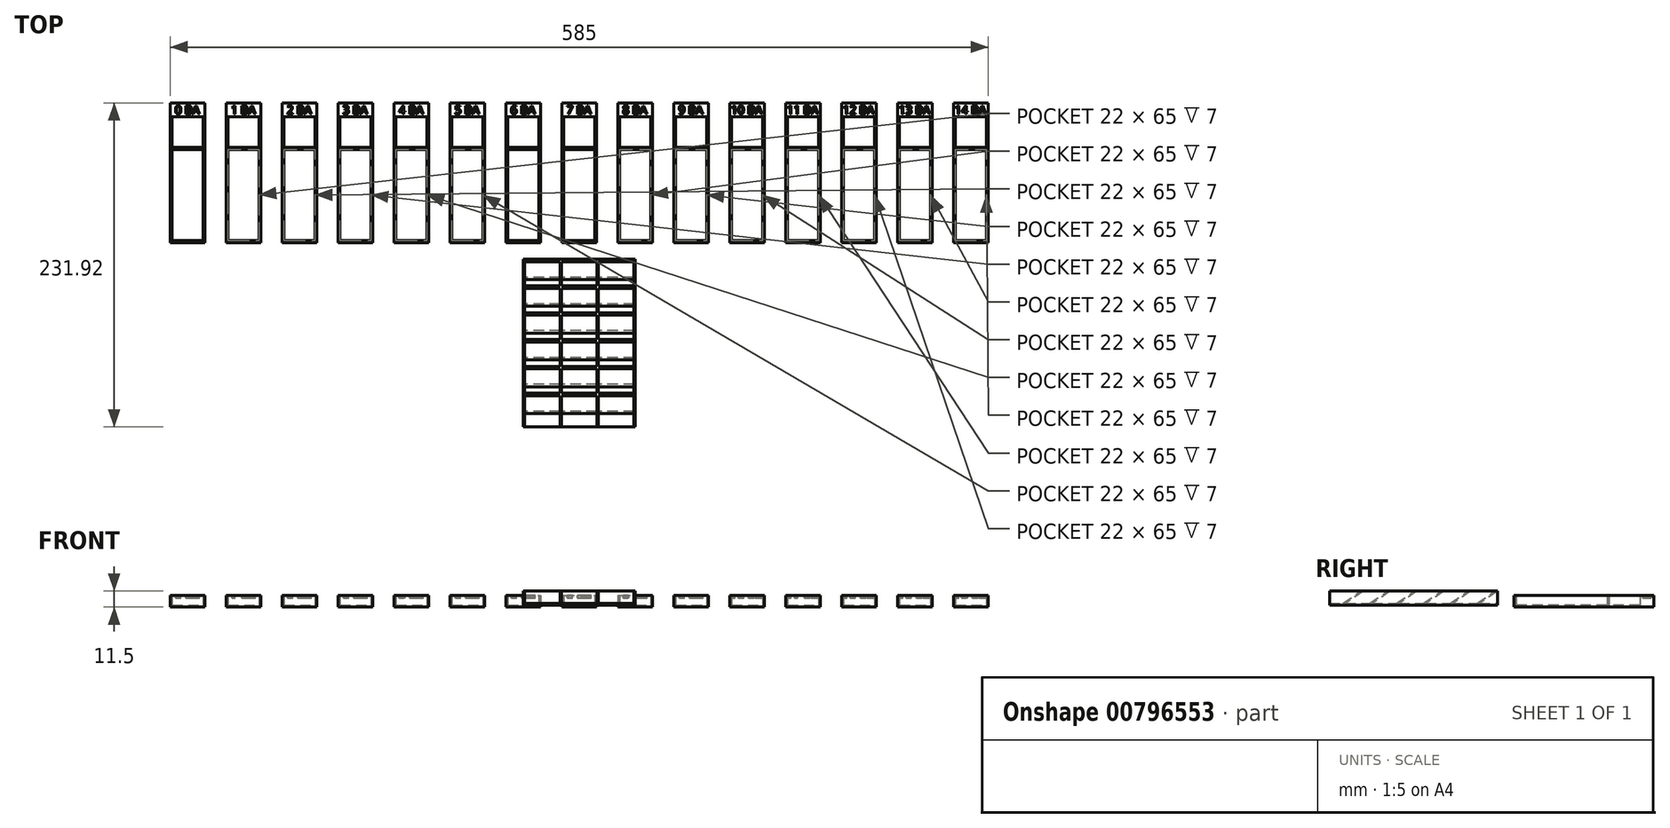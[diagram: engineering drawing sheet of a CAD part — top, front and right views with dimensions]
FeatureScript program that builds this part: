
annotation { "Feature Type Name" : "Feature", "Feature Type Description" : "" }
export const myFeature = defineFeature(function(context is Context, id is Id, definition is map)
    precondition{}
    {
        {
            var Q0;
            Q0=qCreatedBy(makeId("Top.planeOp"),FACE);
            var sketch = newSketch(context, id + "F0", { "sketchPlane" : qUnion([Q0])});
            skLineSegment(sketch, "E0.bottom", {"start": v(30.55, 66.22) * mm, "end": v(55.55, 66.22) * mm});
            skLineSegment(sketch, "E0.top", {"start": v(30.55, -33.78) * mm, "end": v(55.55, -33.78) * mm});
            skLineSegment(sketch, "E0.left", {"start": v(30.55, 66.22) * mm, "end": v(30.55, -33.78) * mm});
            skLineSegment(sketch, "E0.right", {"start": v(55.55, 66.22) * mm, "end": v(55.55, -33.78) * mm});
            skLineSegment(sketch, "E1.bottom", {"start": v(32.05, 56.22) * mm, "end": v(54.05, 56.22) * mm});
            skLineSegment(sketch, "E1.top", {"start": v(32.05, 34.22) * mm, "end": v(54.05, 34.22) * mm});
            skLineSegment(sketch, "E1.left", {"start": v(32.05, 56.22) * mm, "end": v(32.05, 34.22) * mm});
            skLineSegment(sketch, "E1.right", {"start": v(54.05, 56.22) * mm, "end": v(54.05, 34.22) * mm});
            skLineSegment(sketch, "E2.bottom", {"start": v(42.3, 32.72) * mm, "end": v(43.8, 32.72) * mm});
            skLineSegment(sketch, "E2.top", {"start": v(42.3, -32.28) * mm, "end": v(43.8, -32.28) * mm});
            skLineSegment(sketch, "E2.left", {"start": v(42.3, 32.72) * mm, "end": v(42.3, -32.28) * mm});
            skLineSegment(sketch, "E2.right", {"start": v(43.8, 32.72) * mm, "end": v(43.8, -32.28) * mm});
            skLineSegment(sketch, "E3.bottom", {"start": v(32.05, 32.72) * mm, "end": v(54.05, 32.72) * mm});
            skLineSegment(sketch, "E3.top", {"start": v(32.05, -32.28) * mm, "end": v(54.05, -32.28) * mm});
            skLineSegment(sketch, "E3.left", {"start": v(32.05, 32.72) * mm, "end": v(32.05, -32.28) * mm});
            skLineSegment(sketch, "E3.right", {"start": v(54.05, 32.72) * mm, "end": v(54.05, -32.28) * mm});
            skLineSegment(sketch, "E4", {"start": v(43.05, 66.22) * mm, "end": v(43.05, -33.78) * mm, "construction": true});
            skLineSegment(sketch, "E5.1.0.0", {"start": v(72.05, 34.22) * mm, "end": v(94.05, 34.22) * mm});
            skLineSegment(sketch, "E5.1.0.1", {"start": v(72.05, 56.22) * mm, "end": v(72.05, 34.22) * mm});
            skLineSegment(sketch, "E5.1.0.2", {"start": v(72.05, 32.72) * mm, "end": v(72.05, -32.28) * mm});
            skLineSegment(sketch, "E5.1.0.3", {"start": v(70.55, 66.22) * mm, "end": v(70.55, -33.78) * mm});
            skLineSegment(sketch, "E5.1.0.4", {"start": v(72.05, -32.28) * mm, "end": v(94.05, -32.28) * mm});
            skLineSegment(sketch, "E5.1.0.5", {"start": v(94.05, 32.72) * mm, "end": v(94.05, -32.28) * mm});
            skLineSegment(sketch, "E5.1.0.6", {"start": v(82.3, 32.72) * mm, "end": v(82.3, -32.28) * mm});
            skLineSegment(sketch, "E5.1.0.7", {"start": v(95.55, 66.22) * mm, "end": v(95.55, -33.78) * mm});
            skLineSegment(sketch, "E5.1.0.8", {"start": v(94.05, 56.22) * mm, "end": v(94.05, 34.22) * mm});
            skLineSegment(sketch, "E5.1.0.9", {"start": v(83.05, 66.22) * mm, "end": v(83.05, -33.78) * mm, "construction": true});
            skLineSegment(sketch, "E5.1.0.10", {"start": v(72.05, 32.72) * mm, "end": v(94.05, 32.72) * mm});
            skLineSegment(sketch, "E5.1.0.11", {"start": v(70.55, 66.22) * mm, "end": v(95.55, 66.22) * mm});
            skLineSegment(sketch, "E5.1.0.12", {"start": v(70.55, -33.78) * mm, "end": v(95.55, -33.78) * mm});
            skLineSegment(sketch, "E5.1.0.13", {"start": v(72.05, 56.22) * mm, "end": v(94.05, 56.22) * mm});
            skLineSegment(sketch, "E5.1.0.14", {"start": v(83.8, 32.72) * mm, "end": v(83.8, -32.28) * mm});
            skLineSegment(sketch, "E5.1.0.15", {"start": v(82.3, -32.28) * mm, "end": v(83.8, -32.28) * mm});
            skLineSegment(sketch, "E5.1.0.16", {"start": v(82.3, 32.72) * mm, "end": v(83.8, 32.72) * mm});
            skLineSegment(sketch, "E5.2.0.0", {"start": v(112.05, 34.22) * mm, "end": v(134.05, 34.22) * mm});
            skLineSegment(sketch, "E5.2.0.1", {"start": v(112.05, 56.22) * mm, "end": v(112.05, 34.22) * mm});
            skLineSegment(sketch, "E5.2.0.2", {"start": v(112.05, 32.72) * mm, "end": v(112.05, -32.28) * mm});
            skLineSegment(sketch, "E5.2.0.3", {"start": v(110.55, 66.22) * mm, "end": v(110.55, -33.78) * mm});
            skLineSegment(sketch, "E5.2.0.4", {"start": v(112.05, -32.28) * mm, "end": v(134.05, -32.28) * mm});
            skLineSegment(sketch, "E5.2.0.5", {"start": v(134.05, 32.72) * mm, "end": v(134.05, -32.28) * mm});
            skLineSegment(sketch, "E5.2.0.6", {"start": v(122.3, 32.72) * mm, "end": v(122.3, -32.28) * mm});
            skLineSegment(sketch, "E5.2.0.7", {"start": v(135.55, 66.22) * mm, "end": v(135.55, -33.78) * mm});
            skLineSegment(sketch, "E5.2.0.8", {"start": v(134.05, 56.22) * mm, "end": v(134.05, 34.22) * mm});
            skLineSegment(sketch, "E5.2.0.9", {"start": v(123.05, 66.22) * mm, "end": v(123.05, -33.78) * mm, "construction": true});
            skLineSegment(sketch, "E5.2.0.10", {"start": v(112.05, 32.72) * mm, "end": v(134.05, 32.72) * mm});
            skLineSegment(sketch, "E5.2.0.11", {"start": v(110.55, 66.22) * mm, "end": v(135.55, 66.22) * mm});
            skLineSegment(sketch, "E5.2.0.12", {"start": v(110.55, -33.78) * mm, "end": v(135.55, -33.78) * mm});
            skLineSegment(sketch, "E5.2.0.13", {"start": v(112.05, 56.22) * mm, "end": v(134.05, 56.22) * mm});
            skLineSegment(sketch, "E5.2.0.14", {"start": v(123.8, 32.72) * mm, "end": v(123.8, -32.28) * mm});
            skLineSegment(sketch, "E5.2.0.15", {"start": v(122.3, -32.28) * mm, "end": v(123.8, -32.28) * mm});
            skLineSegment(sketch, "E5.2.0.16", {"start": v(122.3, 32.72) * mm, "end": v(123.8, 32.72) * mm});
            skLineSegment(sketch, "E5.direction1", {"start": v(30.55, -33.78) * mm, "end": v(70.55, -33.78) * mm, "construction": true});
            skLineSegment(sketch, "E6.0.3.0", {"start": v(152.05, 34.22) * mm, "end": v(174.05, 34.22) * mm});
            skLineSegment(sketch, "E6.3.3.0", {"start": v(152.05, 56.22) * mm, "end": v(152.05, 34.22) * mm});
            skLineSegment(sketch, "E6.6.3.0", {"start": v(152.05, 32.72) * mm, "end": v(152.05, -32.28) * mm});
            skLineSegment(sketch, "E6.9.3.0", {"start": v(150.55, 66.22) * mm, "end": v(150.55, -33.78) * mm});
            skLineSegment(sketch, "E6.12.3.0", {"start": v(152.05, -32.28) * mm, "end": v(174.05, -32.28) * mm});
            skLineSegment(sketch, "E6.15.3.0", {"start": v(174.05, 32.72) * mm, "end": v(174.05, -32.28) * mm});
            skLineSegment(sketch, "E6.18.3.0", {"start": v(162.3, 32.72) * mm, "end": v(162.3, -32.28) * mm});
            skLineSegment(sketch, "E6.21.3.0", {"start": v(175.55, 66.22) * mm, "end": v(175.55, -33.78) * mm});
            skLineSegment(sketch, "E6.24.3.0", {"start": v(174.05, 56.22) * mm, "end": v(174.05, 34.22) * mm});
            skLineSegment(sketch, "E6.27.3.0", {"start": v(163.05, 66.22) * mm, "end": v(163.05, -33.78) * mm, "construction": true});
            skLineSegment(sketch, "E6.30.3.0", {"start": v(152.05, 32.72) * mm, "end": v(174.05, 32.72) * mm});
            skLineSegment(sketch, "E6.33.3.0", {"start": v(150.55, 66.22) * mm, "end": v(175.55, 66.22) * mm});
            skLineSegment(sketch, "E6.36.3.0", {"start": v(150.55, -33.78) * mm, "end": v(175.55, -33.78) * mm});
            skLineSegment(sketch, "E6.39.3.0", {"start": v(152.05, 56.22) * mm, "end": v(174.05, 56.22) * mm});
            skLineSegment(sketch, "E6.42.3.0", {"start": v(163.8, 32.72) * mm, "end": v(163.8, -32.28) * mm});
            skLineSegment(sketch, "E6.45.3.0", {"start": v(162.3, -32.28) * mm, "end": v(163.8, -32.28) * mm});
            skLineSegment(sketch, "E6.48.3.0", {"start": v(162.3, 32.72) * mm, "end": v(163.8, 32.72) * mm});
            skLineSegment(sketch, "E6.0.4.0", {"start": v(192.05, 34.22) * mm, "end": v(214.05, 34.22) * mm});
            skLineSegment(sketch, "E6.3.4.0", {"start": v(192.05, 56.22) * mm, "end": v(192.05, 34.22) * mm});
            skLineSegment(sketch, "E6.6.4.0", {"start": v(192.05, 32.72) * mm, "end": v(192.05, -32.28) * mm});
            skLineSegment(sketch, "E6.9.4.0", {"start": v(190.55, 66.22) * mm, "end": v(190.55, -33.78) * mm});
            skLineSegment(sketch, "E6.12.4.0", {"start": v(192.05, -32.28) * mm, "end": v(214.05, -32.28) * mm});
            skLineSegment(sketch, "E6.15.4.0", {"start": v(214.05, 32.72) * mm, "end": v(214.05, -32.28) * mm});
            skLineSegment(sketch, "E6.18.4.0", {"start": v(202.3, 32.72) * mm, "end": v(202.3, -32.28) * mm});
            skLineSegment(sketch, "E6.21.4.0", {"start": v(215.55, 66.22) * mm, "end": v(215.55, -33.78) * mm});
            skLineSegment(sketch, "E6.24.4.0", {"start": v(214.05, 56.22) * mm, "end": v(214.05, 34.22) * mm});
            skLineSegment(sketch, "E6.27.4.0", {"start": v(203.05, 66.22) * mm, "end": v(203.05, -33.78) * mm, "construction": true});
            skLineSegment(sketch, "E6.30.4.0", {"start": v(192.05, 32.72) * mm, "end": v(214.05, 32.72) * mm});
            skLineSegment(sketch, "E6.33.4.0", {"start": v(190.55, 66.22) * mm, "end": v(215.55, 66.22) * mm});
            skLineSegment(sketch, "E6.36.4.0", {"start": v(190.55, -33.78) * mm, "end": v(215.55, -33.78) * mm});
            skLineSegment(sketch, "E6.39.4.0", {"start": v(192.05, 56.22) * mm, "end": v(214.05, 56.22) * mm});
            skLineSegment(sketch, "E6.42.4.0", {"start": v(203.8, 32.72) * mm, "end": v(203.8, -32.28) * mm});
            skLineSegment(sketch, "E6.45.4.0", {"start": v(202.3, -32.28) * mm, "end": v(203.8, -32.28) * mm});
            skLineSegment(sketch, "E6.48.4.0", {"start": v(202.3, 32.72) * mm, "end": v(203.8, 32.72) * mm});
            skLineSegment(sketch, "E6.0.5.0", {"start": v(232.05, 34.22) * mm, "end": v(254.05, 34.22) * mm});
            skLineSegment(sketch, "E6.3.5.0", {"start": v(232.05, 56.22) * mm, "end": v(232.05, 34.22) * mm});
            skLineSegment(sketch, "E6.6.5.0", {"start": v(232.05, 32.72) * mm, "end": v(232.05, -32.28) * mm});
            skLineSegment(sketch, "E6.9.5.0", {"start": v(230.55, 66.22) * mm, "end": v(230.55, -33.78) * mm});
            skLineSegment(sketch, "E6.12.5.0", {"start": v(232.05, -32.28) * mm, "end": v(254.05, -32.28) * mm});
            skLineSegment(sketch, "E6.15.5.0", {"start": v(254.05, 32.72) * mm, "end": v(254.05, -32.28) * mm});
            skLineSegment(sketch, "E6.18.5.0", {"start": v(242.3, 32.72) * mm, "end": v(242.3, -32.28) * mm});
            skLineSegment(sketch, "E6.21.5.0", {"start": v(255.55, 66.22) * mm, "end": v(255.55, -33.78) * mm});
            skLineSegment(sketch, "E6.24.5.0", {"start": v(254.05, 56.22) * mm, "end": v(254.05, 34.22) * mm});
            skLineSegment(sketch, "E6.27.5.0", {"start": v(243.05, 66.22) * mm, "end": v(243.05, -33.78) * mm, "construction": true});
            skLineSegment(sketch, "E6.30.5.0", {"start": v(232.05, 32.72) * mm, "end": v(254.05, 32.72) * mm});
            skLineSegment(sketch, "E6.33.5.0", {"start": v(230.55, 66.22) * mm, "end": v(255.55, 66.22) * mm});
            skLineSegment(sketch, "E6.36.5.0", {"start": v(230.55, -33.78) * mm, "end": v(255.55, -33.78) * mm});
            skLineSegment(sketch, "E6.39.5.0", {"start": v(232.05, 56.22) * mm, "end": v(254.05, 56.22) * mm});
            skLineSegment(sketch, "E6.42.5.0", {"start": v(243.8, 32.72) * mm, "end": v(243.8, -32.28) * mm});
            skLineSegment(sketch, "E6.45.5.0", {"start": v(242.3, -32.28) * mm, "end": v(243.8, -32.28) * mm});
            skLineSegment(sketch, "E6.48.5.0", {"start": v(242.3, 32.72) * mm, "end": v(243.8, 32.72) * mm});
            skLineSegment(sketch, "E6.0.6.0", {"start": v(272.05, 34.22) * mm, "end": v(294.05, 34.22) * mm});
            skLineSegment(sketch, "E6.3.6.0", {"start": v(272.05, 56.22) * mm, "end": v(272.05, 34.22) * mm});
            skLineSegment(sketch, "E6.6.6.0", {"start": v(272.05, 32.72) * mm, "end": v(272.05, -32.28) * mm});
            skLineSegment(sketch, "E6.9.6.0", {"start": v(270.55, 66.22) * mm, "end": v(270.55, -33.78) * mm});
            skLineSegment(sketch, "E6.12.6.0", {"start": v(272.05, -32.28) * mm, "end": v(294.05, -32.28) * mm});
            skLineSegment(sketch, "E6.15.6.0", {"start": v(294.05, 32.72) * mm, "end": v(294.05, -32.28) * mm});
            skLineSegment(sketch, "E6.18.6.0", {"start": v(282.3, 32.72) * mm, "end": v(282.3, -32.28) * mm});
            skLineSegment(sketch, "E6.21.6.0", {"start": v(295.55, 66.22) * mm, "end": v(295.55, -33.78) * mm});
            skLineSegment(sketch, "E6.24.6.0", {"start": v(294.05, 56.22) * mm, "end": v(294.05, 34.22) * mm});
            skLineSegment(sketch, "E6.27.6.0", {"start": v(283.05, 66.22) * mm, "end": v(283.05, -33.78) * mm, "construction": true});
            skLineSegment(sketch, "E6.30.6.0", {"start": v(272.05, 32.72) * mm, "end": v(294.05, 32.72) * mm});
            skLineSegment(sketch, "E6.33.6.0", {"start": v(270.55, 66.22) * mm, "end": v(295.55, 66.22) * mm});
            skLineSegment(sketch, "E6.36.6.0", {"start": v(270.55, -33.78) * mm, "end": v(295.55, -33.78) * mm});
            skLineSegment(sketch, "E6.39.6.0", {"start": v(272.05, 56.22) * mm, "end": v(294.05, 56.22) * mm});
            skLineSegment(sketch, "E6.42.6.0", {"start": v(283.8, 32.72) * mm, "end": v(283.8, -32.28) * mm});
            skLineSegment(sketch, "E6.45.6.0", {"start": v(282.3, -32.28) * mm, "end": v(283.8, -32.28) * mm});
            skLineSegment(sketch, "E6.48.6.0", {"start": v(282.3, 32.72) * mm, "end": v(283.8, 32.72) * mm});
            skLineSegment(sketch, "E6.0.7.0", {"start": v(312.05, 34.22) * mm, "end": v(334.05, 34.22) * mm});
            skLineSegment(sketch, "E6.3.7.0", {"start": v(312.05, 56.22) * mm, "end": v(312.05, 34.22) * mm});
            skLineSegment(sketch, "E6.6.7.0", {"start": v(312.05, 32.72) * mm, "end": v(312.05, -32.28) * mm});
            skLineSegment(sketch, "E6.9.7.0", {"start": v(310.55, 66.22) * mm, "end": v(310.55, -33.78) * mm});
            skLineSegment(sketch, "E6.12.7.0", {"start": v(312.05, -32.28) * mm, "end": v(334.05, -32.28) * mm});
            skLineSegment(sketch, "E6.15.7.0", {"start": v(334.05, 32.72) * mm, "end": v(334.05, -32.28) * mm});
            skLineSegment(sketch, "E6.18.7.0", {"start": v(322.3, 32.72) * mm, "end": v(322.3, -32.28) * mm});
            skLineSegment(sketch, "E6.21.7.0", {"start": v(335.55, 66.22) * mm, "end": v(335.55, -33.78) * mm});
            skLineSegment(sketch, "E6.24.7.0", {"start": v(334.05, 56.22) * mm, "end": v(334.05, 34.22) * mm});
            skLineSegment(sketch, "E6.27.7.0", {"start": v(323.05, 66.22) * mm, "end": v(323.05, -33.78) * mm, "construction": true});
            skLineSegment(sketch, "E6.30.7.0", {"start": v(312.05, 32.72) * mm, "end": v(334.05, 32.72) * mm});
            skLineSegment(sketch, "E6.33.7.0", {"start": v(310.55, 66.22) * mm, "end": v(335.55, 66.22) * mm});
            skLineSegment(sketch, "E6.36.7.0", {"start": v(310.55, -33.78) * mm, "end": v(335.55, -33.78) * mm});
            skLineSegment(sketch, "E6.39.7.0", {"start": v(312.05, 56.22) * mm, "end": v(334.05, 56.22) * mm});
            skLineSegment(sketch, "E6.42.7.0", {"start": v(323.8, 32.72) * mm, "end": v(323.8, -32.28) * mm});
            skLineSegment(sketch, "E6.45.7.0", {"start": v(322.3, -32.28) * mm, "end": v(323.8, -32.28) * mm});
            skLineSegment(sketch, "E6.48.7.0", {"start": v(322.3, 32.72) * mm, "end": v(323.8, 32.72) * mm});
            skLineSegment(sketch, "E6.0.8.0", {"start": v(352.05, 34.22) * mm, "end": v(374.05, 34.22) * mm});
            skLineSegment(sketch, "E6.3.8.0", {"start": v(352.05, 56.22) * mm, "end": v(352.05, 34.22) * mm});
            skLineSegment(sketch, "E6.6.8.0", {"start": v(352.05, 32.72) * mm, "end": v(352.05, -32.28) * mm});
            skLineSegment(sketch, "E6.9.8.0", {"start": v(350.55, 66.22) * mm, "end": v(350.55, -33.78) * mm});
            skLineSegment(sketch, "E6.12.8.0", {"start": v(352.05, -32.28) * mm, "end": v(374.05, -32.28) * mm});
            skLineSegment(sketch, "E6.15.8.0", {"start": v(374.05, 32.72) * mm, "end": v(374.05, -32.28) * mm});
            skLineSegment(sketch, "E6.18.8.0", {"start": v(362.3, 32.72) * mm, "end": v(362.3, -32.28) * mm});
            skLineSegment(sketch, "E6.21.8.0", {"start": v(375.55, 66.22) * mm, "end": v(375.55, -33.78) * mm});
            skLineSegment(sketch, "E6.24.8.0", {"start": v(374.05, 56.22) * mm, "end": v(374.05, 34.22) * mm});
            skLineSegment(sketch, "E6.27.8.0", {"start": v(363.05, 66.22) * mm, "end": v(363.05, -33.78) * mm, "construction": true});
            skLineSegment(sketch, "E6.30.8.0", {"start": v(352.05, 32.72) * mm, "end": v(374.05, 32.72) * mm});
            skLineSegment(sketch, "E6.33.8.0", {"start": v(350.55, 66.22) * mm, "end": v(375.55, 66.22) * mm});
            skLineSegment(sketch, "E6.36.8.0", {"start": v(350.55, -33.78) * mm, "end": v(375.55, -33.78) * mm});
            skLineSegment(sketch, "E6.39.8.0", {"start": v(352.05, 56.22) * mm, "end": v(374.05, 56.22) * mm});
            skLineSegment(sketch, "E6.42.8.0", {"start": v(363.8, 32.72) * mm, "end": v(363.8, -32.28) * mm});
            skLineSegment(sketch, "E6.45.8.0", {"start": v(362.3, -32.28) * mm, "end": v(363.8, -32.28) * mm});
            skLineSegment(sketch, "E6.48.8.0", {"start": v(362.3, 32.72) * mm, "end": v(363.8, 32.72) * mm});
            skLineSegment(sketch, "E6.0.9.0", {"start": v(392.05, 34.22) * mm, "end": v(414.05, 34.22) * mm});
            skLineSegment(sketch, "E6.3.9.0", {"start": v(392.05, 56.22) * mm, "end": v(392.05, 34.22) * mm});
            skLineSegment(sketch, "E6.6.9.0", {"start": v(392.05, 32.72) * mm, "end": v(392.05, -32.28) * mm});
            skLineSegment(sketch, "E6.9.9.0", {"start": v(390.55, 66.22) * mm, "end": v(390.55, -33.78) * mm});
            skLineSegment(sketch, "E6.12.9.0", {"start": v(392.05, -32.28) * mm, "end": v(414.05, -32.28) * mm});
            skLineSegment(sketch, "E6.15.9.0", {"start": v(414.05, 32.72) * mm, "end": v(414.05, -32.28) * mm});
            skLineSegment(sketch, "E6.18.9.0", {"start": v(402.3, 32.72) * mm, "end": v(402.3, -32.28) * mm});
            skLineSegment(sketch, "E6.21.9.0", {"start": v(415.55, 66.22) * mm, "end": v(415.55, -33.78) * mm});
            skLineSegment(sketch, "E6.24.9.0", {"start": v(414.05, 56.22) * mm, "end": v(414.05, 34.22) * mm});
            skLineSegment(sketch, "E6.27.9.0", {"start": v(403.05, 66.22) * mm, "end": v(403.05, -33.78) * mm, "construction": true});
            skLineSegment(sketch, "E6.30.9.0", {"start": v(392.05, 32.72) * mm, "end": v(414.05, 32.72) * mm});
            skLineSegment(sketch, "E6.33.9.0", {"start": v(390.55, 66.22) * mm, "end": v(415.55, 66.22) * mm});
            skLineSegment(sketch, "E6.36.9.0", {"start": v(390.55, -33.78) * mm, "end": v(415.55, -33.78) * mm});
            skLineSegment(sketch, "E6.39.9.0", {"start": v(392.05, 56.22) * mm, "end": v(414.05, 56.22) * mm});
            skLineSegment(sketch, "E6.42.9.0", {"start": v(403.8, 32.72) * mm, "end": v(403.8, -32.28) * mm});
            skLineSegment(sketch, "E6.45.9.0", {"start": v(402.3, -32.28) * mm, "end": v(403.8, -32.28) * mm});
            skLineSegment(sketch, "E6.48.9.0", {"start": v(402.3, 32.72) * mm, "end": v(403.8, 32.72) * mm});
            skLineSegment(sketch, "E6.0.10.0", {"start": v(432.05, 34.22) * mm, "end": v(454.05, 34.22) * mm});
            skLineSegment(sketch, "E6.3.10.0", {"start": v(432.05, 56.22) * mm, "end": v(432.05, 34.22) * mm});
            skLineSegment(sketch, "E6.6.10.0", {"start": v(432.05, 32.72) * mm, "end": v(432.05, -32.28) * mm});
            skLineSegment(sketch, "E6.9.10.0", {"start": v(430.55, 66.22) * mm, "end": v(430.55, -33.78) * mm});
            skLineSegment(sketch, "E6.12.10.0", {"start": v(432.05, -32.28) * mm, "end": v(454.05, -32.28) * mm});
            skLineSegment(sketch, "E6.15.10.0", {"start": v(454.05, 32.72) * mm, "end": v(454.05, -32.28) * mm});
            skLineSegment(sketch, "E6.18.10.0", {"start": v(442.3, 32.72) * mm, "end": v(442.3, -32.28) * mm});
            skLineSegment(sketch, "E6.21.10.0", {"start": v(455.55, 66.22) * mm, "end": v(455.55, -33.78) * mm});
            skLineSegment(sketch, "E6.24.10.0", {"start": v(454.05, 56.22) * mm, "end": v(454.05, 34.22) * mm});
            skLineSegment(sketch, "E6.27.10.0", {"start": v(443.05, 66.22) * mm, "end": v(443.05, -33.78) * mm, "construction": true});
            skLineSegment(sketch, "E6.30.10.0", {"start": v(432.05, 32.72) * mm, "end": v(454.05, 32.72) * mm});
            skLineSegment(sketch, "E6.33.10.0", {"start": v(430.55, 66.22) * mm, "end": v(455.55, 66.22) * mm});
            skLineSegment(sketch, "E6.36.10.0", {"start": v(430.55, -33.78) * mm, "end": v(455.55, -33.78) * mm});
            skLineSegment(sketch, "E6.39.10.0", {"start": v(432.05, 56.22) * mm, "end": v(454.05, 56.22) * mm});
            skLineSegment(sketch, "E6.42.10.0", {"start": v(443.8, 32.72) * mm, "end": v(443.8, -32.28) * mm});
            skLineSegment(sketch, "E6.45.10.0", {"start": v(442.3, -32.28) * mm, "end": v(443.8, -32.28) * mm});
            skLineSegment(sketch, "E6.48.10.0", {"start": v(442.3, 32.72) * mm, "end": v(443.8, 32.72) * mm});
            skLineSegment(sketch, "E6.0.11.0", {"start": v(472.05, 34.22) * mm, "end": v(494.05, 34.22) * mm});
            skLineSegment(sketch, "E6.3.11.0", {"start": v(472.05, 56.22) * mm, "end": v(472.05, 34.22) * mm});
            skLineSegment(sketch, "E6.6.11.0", {"start": v(472.05, 32.72) * mm, "end": v(472.05, -32.28) * mm});
            skLineSegment(sketch, "E6.9.11.0", {"start": v(470.55, 66.22) * mm, "end": v(470.55, -33.78) * mm});
            skLineSegment(sketch, "E6.12.11.0", {"start": v(472.05, -32.28) * mm, "end": v(494.05, -32.28) * mm});
            skLineSegment(sketch, "E6.15.11.0", {"start": v(494.05, 32.72) * mm, "end": v(494.05, -32.28) * mm});
            skLineSegment(sketch, "E6.18.11.0", {"start": v(482.3, 32.72) * mm, "end": v(482.3, -32.28) * mm});
            skLineSegment(sketch, "E6.21.11.0", {"start": v(495.55, 66.22) * mm, "end": v(495.55, -33.78) * mm});
            skLineSegment(sketch, "E6.24.11.0", {"start": v(494.05, 56.22) * mm, "end": v(494.05, 34.22) * mm});
            skLineSegment(sketch, "E6.27.11.0", {"start": v(483.05, 66.22) * mm, "end": v(483.05, -33.78) * mm, "construction": true});
            skLineSegment(sketch, "E6.30.11.0", {"start": v(472.05, 32.72) * mm, "end": v(494.05, 32.72) * mm});
            skLineSegment(sketch, "E6.33.11.0", {"start": v(470.55, 66.22) * mm, "end": v(495.55, 66.22) * mm});
            skLineSegment(sketch, "E6.36.11.0", {"start": v(470.55, -33.78) * mm, "end": v(495.55, -33.78) * mm});
            skLineSegment(sketch, "E6.39.11.0", {"start": v(472.05, 56.22) * mm, "end": v(494.05, 56.22) * mm});
            skLineSegment(sketch, "E6.42.11.0", {"start": v(483.8, 32.72) * mm, "end": v(483.8, -32.28) * mm});
            skLineSegment(sketch, "E6.45.11.0", {"start": v(482.3, -32.28) * mm, "end": v(483.8, -32.28) * mm});
            skLineSegment(sketch, "E6.48.11.0", {"start": v(482.3, 32.72) * mm, "end": v(483.8, 32.72) * mm});
            skLineSegment(sketch, "E7.0.12.0", {"start": v(512.05, 34.22) * mm, "end": v(534.05, 34.22) * mm});
            skLineSegment(sketch, "E7.3.12.0", {"start": v(512.05, 56.22) * mm, "end": v(512.05, 34.22) * mm});
            skLineSegment(sketch, "E7.6.12.0", {"start": v(512.05, 32.72) * mm, "end": v(512.05, -32.28) * mm});
            skLineSegment(sketch, "E7.9.12.0", {"start": v(510.55, 66.22) * mm, "end": v(510.55, -33.78) * mm});
            skLineSegment(sketch, "E7.12.12.0", {"start": v(512.05, -32.28) * mm, "end": v(534.05, -32.28) * mm});
            skLineSegment(sketch, "E7.15.12.0", {"start": v(534.05, 32.72) * mm, "end": v(534.05, -32.28) * mm});
            skLineSegment(sketch, "E7.18.12.0", {"start": v(522.3, 32.72) * mm, "end": v(522.3, -32.28) * mm});
            skLineSegment(sketch, "E7.21.12.0", {"start": v(535.55, 66.22) * mm, "end": v(535.55, -33.78) * mm});
            skLineSegment(sketch, "E7.24.12.0", {"start": v(534.05, 56.22) * mm, "end": v(534.05, 34.22) * mm});
            skLineSegment(sketch, "E7.27.12.0", {"start": v(523.05, 66.22) * mm, "end": v(523.05, -33.78) * mm, "construction": true});
            skLineSegment(sketch, "E7.30.12.0", {"start": v(512.05, 32.72) * mm, "end": v(534.05, 32.72) * mm});
            skLineSegment(sketch, "E7.33.12.0", {"start": v(510.55, 66.22) * mm, "end": v(535.55, 66.22) * mm});
            skLineSegment(sketch, "E7.36.12.0", {"start": v(510.55, -33.78) * mm, "end": v(535.55, -33.78) * mm});
            skLineSegment(sketch, "E7.39.12.0", {"start": v(512.05, 56.22) * mm, "end": v(534.05, 56.22) * mm});
            skLineSegment(sketch, "E7.42.12.0", {"start": v(523.8, 32.72) * mm, "end": v(523.8, -32.28) * mm});
            skLineSegment(sketch, "E7.45.12.0", {"start": v(522.3, -32.28) * mm, "end": v(523.8, -32.28) * mm});
            skLineSegment(sketch, "E7.48.12.0", {"start": v(522.3, 32.72) * mm, "end": v(523.8, 32.72) * mm});
            skLineSegment(sketch, "E8.0.13.0", {"start": v(552.05, 34.22) * mm, "end": v(574.05, 34.22) * mm});
            skLineSegment(sketch, "E8.3.13.0", {"start": v(552.05, 56.22) * mm, "end": v(552.05, 34.22) * mm});
            skLineSegment(sketch, "E8.6.13.0", {"start": v(552.05, 32.72) * mm, "end": v(552.05, -32.28) * mm});
            skLineSegment(sketch, "E8.9.13.0", {"start": v(550.55, 66.22) * mm, "end": v(550.55, -33.78) * mm});
            skLineSegment(sketch, "E8.12.13.0", {"start": v(552.05, -32.28) * mm, "end": v(574.05, -32.28) * mm});
            skLineSegment(sketch, "E8.15.13.0", {"start": v(574.05, 32.72) * mm, "end": v(574.05, -32.28) * mm});
            skLineSegment(sketch, "E8.18.13.0", {"start": v(562.3, 32.72) * mm, "end": v(562.3, -32.28) * mm});
            skLineSegment(sketch, "E8.21.13.0", {"start": v(575.55, 66.22) * mm, "end": v(575.55, -33.78) * mm});
            skLineSegment(sketch, "E8.24.13.0", {"start": v(574.05, 56.22) * mm, "end": v(574.05, 34.22) * mm});
            skLineSegment(sketch, "E8.27.13.0", {"start": v(563.05, 66.22) * mm, "end": v(563.05, -33.78) * mm, "construction": true});
            skLineSegment(sketch, "E8.30.13.0", {"start": v(552.05, 32.72) * mm, "end": v(574.05, 32.72) * mm});
            skLineSegment(sketch, "E8.33.13.0", {"start": v(550.55, 66.22) * mm, "end": v(575.55, 66.22) * mm});
            skLineSegment(sketch, "E8.36.13.0", {"start": v(550.55, -33.78) * mm, "end": v(575.55, -33.78) * mm});
            skLineSegment(sketch, "E8.39.13.0", {"start": v(552.05, 56.22) * mm, "end": v(574.05, 56.22) * mm});
            skLineSegment(sketch, "E8.42.13.0", {"start": v(563.8, 32.72) * mm, "end": v(563.8, -32.28) * mm});
            skLineSegment(sketch, "E8.45.13.0", {"start": v(562.3, -32.28) * mm, "end": v(563.8, -32.28) * mm});
            skLineSegment(sketch, "E8.48.13.0", {"start": v(562.3, 32.72) * mm, "end": v(563.8, 32.72) * mm});
            skLineSegment(sketch, "E8.0.14.0", {"start": v(592.05, 34.22) * mm, "end": v(614.05, 34.22) * mm});
            skLineSegment(sketch, "E8.3.14.0", {"start": v(592.05, 56.22) * mm, "end": v(592.05, 34.22) * mm});
            skLineSegment(sketch, "E8.6.14.0", {"start": v(592.05, 32.72) * mm, "end": v(592.05, -32.28) * mm});
            skLineSegment(sketch, "E8.9.14.0", {"start": v(590.55, 66.22) * mm, "end": v(590.55, -33.78) * mm});
            skLineSegment(sketch, "E8.12.14.0", {"start": v(592.05, -32.28) * mm, "end": v(614.05, -32.28) * mm});
            skLineSegment(sketch, "E8.15.14.0", {"start": v(614.05, 32.72) * mm, "end": v(614.05, -32.28) * mm});
            skLineSegment(sketch, "E8.18.14.0", {"start": v(602.3, 32.72) * mm, "end": v(602.3, -32.28) * mm});
            skLineSegment(sketch, "E8.21.14.0", {"start": v(615.55, 66.22) * mm, "end": v(615.55, -33.78) * mm});
            skLineSegment(sketch, "E8.24.14.0", {"start": v(614.05, 56.22) * mm, "end": v(614.05, 34.22) * mm});
            skLineSegment(sketch, "E8.27.14.0", {"start": v(603.05, 66.22) * mm, "end": v(603.05, -33.78) * mm, "construction": true});
            skLineSegment(sketch, "E8.30.14.0", {"start": v(592.05, 32.72) * mm, "end": v(614.05, 32.72) * mm});
            skLineSegment(sketch, "E8.33.14.0", {"start": v(590.55, 66.22) * mm, "end": v(615.55, 66.22) * mm});
            skLineSegment(sketch, "E8.36.14.0", {"start": v(590.55, -33.78) * mm, "end": v(615.55, -33.78) * mm});
            skLineSegment(sketch, "E8.39.14.0", {"start": v(592.05, 56.22) * mm, "end": v(614.05, 56.22) * mm});
            skLineSegment(sketch, "E8.42.14.0", {"start": v(603.8, 32.72) * mm, "end": v(603.8, -32.28) * mm});
            skLineSegment(sketch, "E8.45.14.0", {"start": v(602.3, -32.28) * mm, "end": v(603.8, -32.28) * mm});
            skLineSegment(sketch, "E8.48.14.0", {"start": v(602.3, 32.72) * mm, "end": v(603.8, 32.72) * mm});
            skSolve(sketch);
        }
        {
            var Q0;
            Q0=qCreatedBy(makeId("Top.planeOp"),FACE);
            var sketch = newSketch(context, id + "F1", { "sketchPlane" : qUnion([Q0])});
            skLineSegment(sketch, "E9.bottom", {"start": v(30.55, 66.22) * mm, "end": v(55.55, 66.22) * mm});
            skLineSegment(sketch, "E9.top", {"start": v(30.55, -33.78) * mm, "end": v(55.55, -33.78) * mm});
            skLineSegment(sketch, "E9.left", {"start": v(30.55, 66.22) * mm, "end": v(30.55, -33.78) * mm});
            skLineSegment(sketch, "E9.right", {"start": v(55.55, 66.22) * mm, "end": v(55.55, -33.78) * mm});
            skLineSegment(sketch, "E10.1.0.0", {"start": v(70.55, 66.22) * mm, "end": v(95.55, 66.22) * mm});
            skLineSegment(sketch, "E10.1.0.1", {"start": v(70.55, 66.22) * mm, "end": v(70.55, -33.78) * mm});
            skLineSegment(sketch, "E10.1.0.2", {"start": v(70.55, -33.78) * mm, "end": v(95.55, -33.78) * mm});
            skLineSegment(sketch, "E10.1.0.3", {"start": v(95.55, 66.22) * mm, "end": v(95.55, -33.78) * mm});
            skLineSegment(sketch, "E10.2.0.0", {"start": v(110.55, 66.22) * mm, "end": v(135.55, 66.22) * mm});
            skLineSegment(sketch, "E10.2.0.1", {"start": v(110.55, 66.22) * mm, "end": v(110.55, -33.78) * mm});
            skLineSegment(sketch, "E10.2.0.2", {"start": v(110.55, -33.78) * mm, "end": v(135.55, -33.78) * mm});
            skLineSegment(sketch, "E10.2.0.3", {"start": v(135.55, 66.22) * mm, "end": v(135.55, -33.78) * mm});
            skLineSegment(sketch, "E10.direction1", {"start": v(30.55, 66.22) * mm, "end": v(70.55, 66.22) * mm, "construction": true});
            skLineSegment(sketch, "E11.0.3.0", {"start": v(150.55, 66.22) * mm, "end": v(175.55, 66.22) * mm});
            skLineSegment(sketch, "E11.3.3.0", {"start": v(150.55, 66.22) * mm, "end": v(150.55, -33.78) * mm});
            skLineSegment(sketch, "E11.6.3.0", {"start": v(150.55, -33.78) * mm, "end": v(175.55, -33.78) * mm});
            skLineSegment(sketch, "E11.9.3.0", {"start": v(175.55, 66.22) * mm, "end": v(175.55, -33.78) * mm});
            skLineSegment(sketch, "E11.0.4.0", {"start": v(190.55, 66.22) * mm, "end": v(215.55, 66.22) * mm});
            skLineSegment(sketch, "E11.3.4.0", {"start": v(190.55, 66.22) * mm, "end": v(190.55, -33.78) * mm});
            skLineSegment(sketch, "E11.6.4.0", {"start": v(190.55, -33.78) * mm, "end": v(215.55, -33.78) * mm});
            skLineSegment(sketch, "E11.9.4.0", {"start": v(215.55, 66.22) * mm, "end": v(215.55, -33.78) * mm});
            skLineSegment(sketch, "E11.0.5.0", {"start": v(230.55, 66.22) * mm, "end": v(255.55, 66.22) * mm});
            skLineSegment(sketch, "E11.3.5.0", {"start": v(230.55, 66.22) * mm, "end": v(230.55, -33.78) * mm});
            skLineSegment(sketch, "E11.6.5.0", {"start": v(230.55, -33.78) * mm, "end": v(255.55, -33.78) * mm});
            skLineSegment(sketch, "E11.9.5.0", {"start": v(255.55, 66.22) * mm, "end": v(255.55, -33.78) * mm});
            skLineSegment(sketch, "E11.0.6.0", {"start": v(270.55, 66.22) * mm, "end": v(295.55, 66.22) * mm});
            skLineSegment(sketch, "E11.3.6.0", {"start": v(270.55, 66.22) * mm, "end": v(270.55, -33.78) * mm});
            skLineSegment(sketch, "E11.6.6.0", {"start": v(270.55, -33.78) * mm, "end": v(295.55, -33.78) * mm});
            skLineSegment(sketch, "E11.9.6.0", {"start": v(295.55, 66.22) * mm, "end": v(295.55, -33.78) * mm});
            skLineSegment(sketch, "E11.0.7.0", {"start": v(310.55, 66.22) * mm, "end": v(335.55, 66.22) * mm});
            skLineSegment(sketch, "E11.3.7.0", {"start": v(310.55, 66.22) * mm, "end": v(310.55, -33.78) * mm});
            skLineSegment(sketch, "E11.6.7.0", {"start": v(310.55, -33.78) * mm, "end": v(335.55, -33.78) * mm});
            skLineSegment(sketch, "E11.9.7.0", {"start": v(335.55, 66.22) * mm, "end": v(335.55, -33.78) * mm});
            skLineSegment(sketch, "E11.0.8.0", {"start": v(350.55, 66.22) * mm, "end": v(375.55, 66.22) * mm});
            skLineSegment(sketch, "E11.3.8.0", {"start": v(350.55, 66.22) * mm, "end": v(350.55, -33.78) * mm});
            skLineSegment(sketch, "E11.6.8.0", {"start": v(350.55, -33.78) * mm, "end": v(375.55, -33.78) * mm});
            skLineSegment(sketch, "E11.9.8.0", {"start": v(375.55, 66.22) * mm, "end": v(375.55, -33.78) * mm});
            skLineSegment(sketch, "E11.0.9.0", {"start": v(390.55, 66.22) * mm, "end": v(415.55, 66.22) * mm});
            skLineSegment(sketch, "E11.3.9.0", {"start": v(390.55, 66.22) * mm, "end": v(390.55, -33.78) * mm});
            skLineSegment(sketch, "E11.6.9.0", {"start": v(390.55, -33.78) * mm, "end": v(415.55, -33.78) * mm});
            skLineSegment(sketch, "E11.9.9.0", {"start": v(415.55, 66.22) * mm, "end": v(415.55, -33.78) * mm});
            skLineSegment(sketch, "E11.0.10.0", {"start": v(430.55, 66.22) * mm, "end": v(455.55, 66.22) * mm});
            skLineSegment(sketch, "E11.3.10.0", {"start": v(430.55, 66.22) * mm, "end": v(430.55, -33.78) * mm});
            skLineSegment(sketch, "E11.6.10.0", {"start": v(430.55, -33.78) * mm, "end": v(455.55, -33.78) * mm});
            skLineSegment(sketch, "E11.9.10.0", {"start": v(455.55, 66.22) * mm, "end": v(455.55, -33.78) * mm});
            skLineSegment(sketch, "E11.0.11.0", {"start": v(470.55, 66.22) * mm, "end": v(495.55, 66.22) * mm});
            skLineSegment(sketch, "E11.3.11.0", {"start": v(470.55, 66.22) * mm, "end": v(470.55, -33.78) * mm});
            skLineSegment(sketch, "E11.6.11.0", {"start": v(470.55, -33.78) * mm, "end": v(495.55, -33.78) * mm});
            skLineSegment(sketch, "E11.9.11.0", {"start": v(495.55, 66.22) * mm, "end": v(495.55, -33.78) * mm});
            skLineSegment(sketch, "E12.0.12.0", {"start": v(510.55, 66.22) * mm, "end": v(535.55, 66.22) * mm});
            skLineSegment(sketch, "E12.3.12.0", {"start": v(510.55, 66.22) * mm, "end": v(510.55, -33.78) * mm});
            skLineSegment(sketch, "E12.6.12.0", {"start": v(510.55, -33.78) * mm, "end": v(535.55, -33.78) * mm});
            skLineSegment(sketch, "E12.9.12.0", {"start": v(535.55, 66.22) * mm, "end": v(535.55, -33.78) * mm});
            skLineSegment(sketch, "E12.0.13.0", {"start": v(550.55, 66.22) * mm, "end": v(575.55, 66.22) * mm});
            skLineSegment(sketch, "E12.3.13.0", {"start": v(550.55, 66.22) * mm, "end": v(550.55, -33.78) * mm});
            skLineSegment(sketch, "E12.6.13.0", {"start": v(550.55, -33.78) * mm, "end": v(575.55, -33.78) * mm});
            skLineSegment(sketch, "E12.9.13.0", {"start": v(575.55, 66.22) * mm, "end": v(575.55, -33.78) * mm});
            skLineSegment(sketch, "E12.0.14.0", {"start": v(590.55, 66.22) * mm, "end": v(615.55, 66.22) * mm});
            skLineSegment(sketch, "E12.3.14.0", {"start": v(590.55, 66.22) * mm, "end": v(590.55, -33.78) * mm});
            skLineSegment(sketch, "E12.6.14.0", {"start": v(590.55, -33.78) * mm, "end": v(615.55, -33.78) * mm});
            skLineSegment(sketch, "E12.9.14.0", {"start": v(615.55, 66.22) * mm, "end": v(615.55, -33.78) * mm});
            skSolve(sketch);
        }
        {
            var Q0;
            {Q0=qUnion([makeQuery(id+"F0.imprint","IMPRINT",FACE,{"disambiguationData":[TD([[makeQuery(id+"F0.imprint","IMPRINT",EDGE,{"derivedFrom":sQuery(id+"F0.wireOp",EDGE,"E0.bottom")}),-1.0]])]}),makeQuery(id+"F0.imprint","IMPRINT",FACE,{"disambiguationData":[TD([[makeQuery(id+"F0.imprint","IMPRINT",EDGE,{"derivedFrom":sQuery(id+"F0.wireOp",EDGE,"E5.1.0.0")}),-1.0]])]}),makeQuery(id+"F0.imprint","IMPRINT",FACE,{"disambiguationData":[TD([[makeQuery(id+"F0.imprint","IMPRINT",EDGE,{"derivedFrom":sQuery(id+"F0.wireOp",EDGE,"E5.2.0.0")}),-1.0]])]}),makeQuery(id+"F0.imprint","IMPRINT",FACE,{"disambiguationData":[TD([[makeQuery(id+"F0.imprint","IMPRINT",EDGE,{"derivedFrom":sQuery(id+"F0.wireOp",EDGE,"E6.0.3.0")}),-1.0]])]}),makeQuery(id+"F0.imprint","IMPRINT",FACE,{"disambiguationData":[TD([[makeQuery(id+"F0.imprint","IMPRINT",EDGE,{"derivedFrom":sQuery(id+"F0.wireOp",EDGE,"E6.0.4.0")}),-1.0]])]}),makeQuery(id+"F0.imprint","IMPRINT",FACE,{"disambiguationData":[TD([[makeQuery(id+"F0.imprint","IMPRINT",EDGE,{"derivedFrom":sQuery(id+"F0.wireOp",EDGE,"E6.0.5.0")}),-1.0]])]}),makeQuery(id+"F0.imprint","IMPRINT",FACE,{"disambiguationData":[TD([[makeQuery(id+"F0.imprint","IMPRINT",EDGE,{"derivedFrom":sQuery(id+"F0.wireOp",EDGE,"E6.0.6.0")}),-1.0]])]}),makeQuery(id+"F0.imprint","IMPRINT",FACE,{"disambiguationData":[TD([[makeQuery(id+"F0.imprint","IMPRINT",EDGE,{"derivedFrom":sQuery(id+"F0.wireOp",EDGE,"E6.0.7.0")}),-1.0]])]}),makeQuery(id+"F0.imprint","IMPRINT",FACE,{"disambiguationData":[TD([[makeQuery(id+"F0.imprint","IMPRINT",EDGE,{"derivedFrom":sQuery(id+"F0.wireOp",EDGE,"E6.0.8.0")}),-1.0]])]}),makeQuery(id+"F0.imprint","IMPRINT",FACE,{"disambiguationData":[TD([[makeQuery(id+"F0.imprint","IMPRINT",EDGE,{"derivedFrom":sQuery(id+"F0.wireOp",EDGE,"E6.0.9.0")}),-1.0]])]}),makeQuery(id+"F0.imprint","IMPRINT",FACE,{"disambiguationData":[TD([[makeQuery(id+"F0.imprint","IMPRINT",EDGE,{"derivedFrom":sQuery(id+"F0.wireOp",EDGE,"E6.0.10.0")}),-1.0]])]}),makeQuery(id+"F0.imprint","IMPRINT",FACE,{"disambiguationData":[TD([[makeQuery(id+"F0.imprint","IMPRINT",EDGE,{"derivedFrom":sQuery(id+"F0.wireOp",EDGE,"E6.0.11.0")}),-1.0]])]}),makeQuery(id+"F0.imprint","IMPRINT",FACE,{"disambiguationData":[TD([[makeQuery(id+"F0.imprint","IMPRINT",EDGE,{"derivedFrom":sQuery(id+"F0.wireOp",EDGE,"E7.0.12.0")}),-1.0]])]}),makeQuery(id+"F0.imprint","IMPRINT",FACE,{"disambiguationData":[TD([[makeQuery(id+"F0.imprint","IMPRINT",EDGE,{"derivedFrom":sQuery(id+"F0.wireOp",EDGE,"E8.0.13.0")}),-1.0]])]}),makeQuery(id+"F0.imprint","IMPRINT",FACE,{"disambiguationData":[TD([[makeQuery(id+"F0.imprint","IMPRINT",EDGE,{"derivedFrom":sQuery(id+"F0.wireOp",EDGE,"E8.0.14.0")}),-1.0]])]})]);}
            extrude(context, id + "F2", {"entities" : qUnion([Q0]), "depth" : 7 * mm, "offsetDistance" : 25 * mm});
        }
        {
            var Q0;
            Q0 = qSketchRegion(id + "F1", true);
            extrude(context, id + "F3", {"entities" : qUnion([Q0]), "operationType" : NewBodyOperationType.ADD, "oppositeDirection" : true, "depth" : 1.5 * mm, "offsetDistance" : 25 * mm});
        }
        {
            var Q0;
            Q0=makeQuery(id+"F2.opExtrude","CAP_FACE",FACE,{"disambiguationData":[OSD([sQuery(id+"F0.wireOp",EDGE,"E0.bottom"),sQuery(id+"F0.wireOp",EDGE,"E0.top"),sQuery(id+"F0.wireOp",EDGE,"E0.left"),sQuery(id+"F0.wireOp",EDGE,"E0.right"),sQuery(id+"F0.wireOp",EDGE,"E1.bottom"),sQuery(id+"F0.wireOp",EDGE,"E1.top"),sQuery(id+"F0.wireOp",EDGE,"E1.left"),sQuery(id+"F0.wireOp",EDGE,"E1.right"),sQuery(id+"F0.wireOp",EDGE,"E2.bottom"),sQuery(id+"F0.wireOp",EDGE,"E2.top"),sQuery(id+"F0.wireOp",EDGE,"E3.bottom"),sQuery(id+"F0.wireOp",EDGE,"E3.top"),sQuery(id+"F0.wireOp",EDGE,"E3.left"),sQuery(id+"F0.wireOp",EDGE,"E3.right")])],"isStart":false});
            var sketch = newSketch(context, id + "F4", { "sketchPlane" : qUnion([Q0])});
            skText(sketch, "E13", { "text": "0 BA", "fontName": "OpenSans-Regular.ttf"});
            const initialGuessF4  = {"E13": [0.03398, 0.05822, 1, 0, 0.006]};
            skSetInitialGuess(sketch, initialGuessF4);
            skSolve(sketch);
        }
        {
            var Q0;
            Q0=makeQuery(id+"F2.opExtrude","CAP_FACE",FACE,{"disambiguationData":[OSD([sQuery(id+"F0.wireOp",EDGE,"E5.1.0.0"),sQuery(id+"F0.wireOp",EDGE,"E5.1.0.1"),sQuery(id+"F0.wireOp",EDGE,"E5.1.0.2"),sQuery(id+"F0.wireOp",EDGE,"E5.1.0.3"),sQuery(id+"F0.wireOp",EDGE,"E5.1.0.4"),sQuery(id+"F0.wireOp",EDGE,"E5.1.0.5"),sQuery(id+"F0.wireOp",EDGE,"E5.1.0.7"),sQuery(id+"F0.wireOp",EDGE,"E5.1.0.8"),sQuery(id+"F0.wireOp",EDGE,"E5.1.0.10"),sQuery(id+"F0.wireOp",EDGE,"E5.1.0.11"),sQuery(id+"F0.wireOp",EDGE,"E5.1.0.12"),sQuery(id+"F0.wireOp",EDGE,"E5.1.0.13")])],"isStart":false});
            var sketch = newSketch(context, id + "F5", { "sketchPlane" : qUnion([Q0])});
            skText(sketch, "E14", { "text": "1 BA", "fontName": "OpenSans-Regular.ttf"});
            const initialGuessF5  = {"E14": [0.07398, 0.05822, 1, 0, 0.006]};
            skSetInitialGuess(sketch, initialGuessF5);
            skSolve(sketch);
        }
        {
            var Q0;
            Q0=makeQuery(id+"F2.opExtrude","CAP_FACE",FACE,{"disambiguationData":[OSD([sQuery(id+"F0.wireOp",EDGE,"E5.2.0.0"),sQuery(id+"F0.wireOp",EDGE,"E5.2.0.1"),sQuery(id+"F0.wireOp",EDGE,"E5.2.0.2"),sQuery(id+"F0.wireOp",EDGE,"E5.2.0.3"),sQuery(id+"F0.wireOp",EDGE,"E5.2.0.4"),sQuery(id+"F0.wireOp",EDGE,"E5.2.0.5"),sQuery(id+"F0.wireOp",EDGE,"E5.2.0.7"),sQuery(id+"F0.wireOp",EDGE,"E5.2.0.8"),sQuery(id+"F0.wireOp",EDGE,"E5.2.0.10"),sQuery(id+"F0.wireOp",EDGE,"E5.2.0.11"),sQuery(id+"F0.wireOp",EDGE,"E5.2.0.12"),sQuery(id+"F0.wireOp",EDGE,"E5.2.0.13")])],"isStart":false});
            var sketch = newSketch(context, id + "F6", { "sketchPlane" : qUnion([Q0])});
            skText(sketch, "E15", { "text": "2 BA", "fontName": "OpenSans-Regular.ttf"});
            const initialGuessF6  = {"E15": [0.11398, 0.05822, 1, 0, 0.006]};
            skSetInitialGuess(sketch, initialGuessF6);
            skSolve(sketch);
        }
        {
            var Q0;
            Q0=makeQuery(id+"F2.opExtrude","CAP_FACE",FACE,{"disambiguationData":[OSD([sQuery(id+"F0.wireOp",EDGE,"E6.0.3.0"),sQuery(id+"F0.wireOp",EDGE,"E6.3.3.0"),sQuery(id+"F0.wireOp",EDGE,"E6.6.3.0"),sQuery(id+"F0.wireOp",EDGE,"E6.9.3.0"),sQuery(id+"F0.wireOp",EDGE,"E6.12.3.0"),sQuery(id+"F0.wireOp",EDGE,"E6.15.3.0"),sQuery(id+"F0.wireOp",EDGE,"E6.21.3.0"),sQuery(id+"F0.wireOp",EDGE,"E6.24.3.0"),sQuery(id+"F0.wireOp",EDGE,"E6.30.3.0"),sQuery(id+"F0.wireOp",EDGE,"E6.33.3.0"),sQuery(id+"F0.wireOp",EDGE,"E6.36.3.0"),sQuery(id+"F0.wireOp",EDGE,"E6.39.3.0")])],"isStart":false});
            var sketch = newSketch(context, id + "F7", { "sketchPlane" : qUnion([Q0])});
            skText(sketch, "E16", { "text": "3 BA", "fontName": "OpenSans-Regular.ttf"});
            const initialGuessF7  = {"E16": [0.15398, 0.05822, 1, 0, 0.006]};
            skSetInitialGuess(sketch, initialGuessF7);
            skSolve(sketch);
        }
        {
            var Q0;
            Q0=makeQuery(id+"F2.opExtrude","CAP_FACE",FACE,{"disambiguationData":[OSD([sQuery(id+"F0.wireOp",EDGE,"E6.0.4.0"),sQuery(id+"F0.wireOp",EDGE,"E6.3.4.0"),sQuery(id+"F0.wireOp",EDGE,"E6.6.4.0"),sQuery(id+"F0.wireOp",EDGE,"E6.9.4.0"),sQuery(id+"F0.wireOp",EDGE,"E6.12.4.0"),sQuery(id+"F0.wireOp",EDGE,"E6.15.4.0"),sQuery(id+"F0.wireOp",EDGE,"E6.21.4.0"),sQuery(id+"F0.wireOp",EDGE,"E6.24.4.0"),sQuery(id+"F0.wireOp",EDGE,"E6.30.4.0"),sQuery(id+"F0.wireOp",EDGE,"E6.33.4.0"),sQuery(id+"F0.wireOp",EDGE,"E6.36.4.0"),sQuery(id+"F0.wireOp",EDGE,"E6.39.4.0")])],"isStart":false});
            var sketch = newSketch(context, id + "F8", { "sketchPlane" : qUnion([Q0])});
            skText(sketch, "E17", { "text": "4 BA", "fontName": "OpenSans-Regular.ttf"});
            const initialGuessF8  = {"E17": [0.19398, 0.05822, 1, 0, 0.006]};
            skSetInitialGuess(sketch, initialGuessF8);
            skSolve(sketch);
        }
        {
            var Q0;
            Q0=makeQuery(id+"F2.opExtrude","CAP_FACE",FACE,{"disambiguationData":[OSD([sQuery(id+"F0.wireOp",EDGE,"E6.0.5.0"),sQuery(id+"F0.wireOp",EDGE,"E6.3.5.0"),sQuery(id+"F0.wireOp",EDGE,"E6.6.5.0"),sQuery(id+"F0.wireOp",EDGE,"E6.9.5.0"),sQuery(id+"F0.wireOp",EDGE,"E6.12.5.0"),sQuery(id+"F0.wireOp",EDGE,"E6.15.5.0"),sQuery(id+"F0.wireOp",EDGE,"E6.21.5.0"),sQuery(id+"F0.wireOp",EDGE,"E6.24.5.0"),sQuery(id+"F0.wireOp",EDGE,"E6.30.5.0"),sQuery(id+"F0.wireOp",EDGE,"E6.33.5.0"),sQuery(id+"F0.wireOp",EDGE,"E6.36.5.0"),sQuery(id+"F0.wireOp",EDGE,"E6.39.5.0")])],"isStart":false});
            var sketch = newSketch(context, id + "F9", { "sketchPlane" : qUnion([Q0])});
            skText(sketch, "E18", { "text": "5 BA", "fontName": "OpenSans-Regular.ttf"});
            skText(sketch, "E19", { "text": "6 BA", "fontName": "OpenSans-Regular.ttf"});
            skText(sketch, "E20", { "text": "7 BA", "fontName": "OpenSans-Regular.ttf"});
            skText(sketch, "E21", { "text": "8 BA", "fontName": "OpenSans-Regular.ttf"});
            skText(sketch, "E22", { "text": "9 BA", "fontName": "OpenSans-Regular.ttf"});
            skText(sketch, "E23", { "text": "10 BA", "fontName": "OpenSans-Regular.ttf"});
            skText(sketch, "E24", { "text": "11 BA", "fontName": "OpenSans-Regular.ttf"});
            skText(sketch, "E25", { "text": "12 BA", "fontName": "OpenSans-Regular.ttf"});
            skText(sketch, "E26", { "text": "13 BA", "fontName": "OpenSans-Regular.ttf"});
            skText(sketch, "E27", { "text": "14 BA", "fontName": "OpenSans-Regular.ttf"});
            const initialGuessF9  = {"E18": [0.23398, 0.05822, 1, 0, 0.006], "E19": [0.27398, 0.05822, 1, 0, 0.006], "E20": [0.31398, 0.05822, 1, 0, 0.006], "E21": [0.35398, 0.05822, 1, 0, 0.006], "E22": [0.39398, 0.05822, 1, 0, 0.006], "E23": [0.4316, 0.05822, 1, 0, 0.006], "E24": [0.4716, 0.05822, 1, 0, 0.006], "E25": [0.5116, 0.05822, 1, 0, 0.006], "E26": [0.5516, 0.05822, 1, 0, 0.006], "E27": [0.5916, 0.05822, 1, 0, 0.006]};
            skSetInitialGuess(sketch, initialGuessF9);
            skSolve(sketch);
        }
        {
            var Q0;
            Q0=makeQuery(id+"F4.imprint","IMPRINT",FACE,{"disambiguationData":[TD([[makeQuery(id+"F4.imprint","IMPRINT",EDGE,{"derivedFrom":sQuery(id+"F4.wireOp",EDGE,"E13.sketch_text.stroke-0")}),-1.0]])]});
            var Q1;
            Q1=makeQuery(id+"F4.imprint","IMPRINT",FACE,{"disambiguationData":[TD([[makeQuery(id+"F4.imprint","IMPRINT",EDGE,{"derivedFrom":sQuery(id+"F4.wireOp",EDGE,"E13.sketch_text.stroke-16")}),-1.0]])]});
            var Q2;
            Q2=makeQuery(id+"F4.imprint","IMPRINT",FACE,{"disambiguationData":[TD([[makeQuery(id+"F4.imprint","IMPRINT",EDGE,{"derivedFrom":sQuery(id+"F4.wireOp",EDGE,"E13.sketch_text.stroke-41")}),-1.0]])]});
            var Q3;
            Q3=makeQuery(id+"F5.imprint","IMPRINT",FACE,{"disambiguationData":[TD([[makeQuery(id+"F5.imprint","IMPRINT",EDGE,{"derivedFrom":sQuery(id+"F5.wireOp",EDGE,"E14.sketch_text.stroke-0")}),-1.0]])]});
            var Q4;
            Q4=makeQuery(id+"F5.imprint","IMPRINT",FACE,{"disambiguationData":[TD([[makeQuery(id+"F5.imprint","IMPRINT",EDGE,{"derivedFrom":sQuery(id+"F5.wireOp",EDGE,"E14.sketch_text.stroke-9")}),-1.0]])]});
            var Q5;
            Q5=makeQuery(id+"F5.imprint","IMPRINT",FACE,{"disambiguationData":[TD([[makeQuery(id+"F5.imprint","IMPRINT",EDGE,{"derivedFrom":sQuery(id+"F5.wireOp",EDGE,"E14.sketch_text.stroke-34")}),-1.0]])]});
            var Q6;
            Q6=makeQuery(id+"F6.imprint","IMPRINT",FACE,{"disambiguationData":[TD([[makeQuery(id+"F6.imprint","IMPRINT",EDGE,{"derivedFrom":sQuery(id+"F6.wireOp",EDGE,"E15.sketch_text.stroke-0")}),-1.0]])]});
            var Q7;
            Q7=makeQuery(id+"F6.imprint","IMPRINT",FACE,{"disambiguationData":[TD([[makeQuery(id+"F6.imprint","IMPRINT",EDGE,{"derivedFrom":sQuery(id+"F6.wireOp",EDGE,"E15.sketch_text.stroke-20")}),-1.0]])]});
            var Q8;
            Q8=makeQuery(id+"F6.imprint","IMPRINT",FACE,{"disambiguationData":[TD([[makeQuery(id+"F6.imprint","IMPRINT",EDGE,{"derivedFrom":sQuery(id+"F6.wireOp",EDGE,"E15.sketch_text.stroke-45")}),-1.0]])]});
            var Q9;
            Q9=makeQuery(id+"F7.imprint","IMPRINT",FACE,{"disambiguationData":[TD([[makeQuery(id+"F7.imprint","IMPRINT",EDGE,{"derivedFrom":sQuery(id+"F7.wireOp",EDGE,"E16.sketch_text.stroke-0")}),-1.0]])]});
            var Q10;
            Q10=makeQuery(id+"F7.imprint","IMPRINT",FACE,{"disambiguationData":[TD([[makeQuery(id+"F7.imprint","IMPRINT",EDGE,{"derivedFrom":sQuery(id+"F7.wireOp",EDGE,"E16.sketch_text.stroke-28")}),-1.0]])]});
            var Q11;
            Q11=makeQuery(id+"F7.imprint","IMPRINT",FACE,{"disambiguationData":[TD([[makeQuery(id+"F7.imprint","IMPRINT",EDGE,{"derivedFrom":sQuery(id+"F7.wireOp",EDGE,"E16.sketch_text.stroke-53")}),-1.0]])]});
            var Q12;
            Q12 = qSketchRegion(id + "F8", true);
            var Q13;
            Q13 = qSketchRegion(id + "F9", true);
            extrude(context, id + "F10", {"entities" : qUnion([Q0, Q1, Q2, Q3, Q4, Q5, Q6, Q7, Q8, Q9, Q10, Q11, Q12, Q13]), "operationType" : NewBodyOperationType.REMOVE, "oppositeDirection" : true, "depth" : 2 * mm, "offsetDistance" : 25 * mm});
        }
        {
            var Q0;
            Q0=qCreatedBy(makeId("Top.planeOp"),FACE);
            var sketch = newSketch(context, id + "F11", { "sketchPlane" : qUnion([Q0])});
            skLineSegment(sketch, "E28.bottom", {"start": v(282.97, -45.7) * mm, "end": v(363.17, -45.7) * mm});
            skLineSegment(sketch, "E28.top", {"start": v(282.97, -165.7) * mm, "end": v(363.17, -165.7) * mm});
            skLineSegment(sketch, "E28.left", {"start": v(282.97, -45.7) * mm, "end": v(282.97, -165.7) * mm});
            skLineSegment(sketch, "E28.right", {"start": v(363.17, -45.7) * mm, "end": v(363.17, -165.7) * mm});
            skLineSegment(sketch, "E29.bottom", {"start": v(309.37, -45.7) * mm, "end": v(310.37, -45.7) * mm});
            skLineSegment(sketch, "E29.top", {"start": v(309.37, -165.7) * mm, "end": v(310.37, -165.7) * mm});
            skLineSegment(sketch, "E29.left", {"start": v(309.37, -45.7) * mm, "end": v(309.37, -165.7) * mm});
            skLineSegment(sketch, "E29.right", {"start": v(310.37, -45.7) * mm, "end": v(310.37, -165.7) * mm});
            skLineSegment(sketch, "E30.bottom", {"start": v(335.77, -45.7) * mm, "end": v(336.77, -45.7) * mm});
            skLineSegment(sketch, "E30.top", {"start": v(335.77, -165.7) * mm, "end": v(336.77, -165.7) * mm});
            skLineSegment(sketch, "E30.left", {"start": v(335.77, -45.7) * mm, "end": v(335.77, -165.7) * mm});
            skLineSegment(sketch, "E30.right", {"start": v(336.77, -45.7) * mm, "end": v(336.77, -165.7) * mm});
            skLineSegment(sketch, "E31.bottom", {"start": v(363.17, -45.7) * mm, "end": v(362.17, -45.7) * mm});
            skLineSegment(sketch, "E31.top", {"start": v(363.17, -165.7) * mm, "end": v(362.17, -165.7) * mm});
            skLineSegment(sketch, "E31.right", {"start": v(362.17, -45.7) * mm, "end": v(362.17, -165.7) * mm});
            skLineSegment(sketch, "E32.bottom", {"start": v(282.97, -45.7) * mm, "end": v(283.97, -45.7) * mm});
            skLineSegment(sketch, "E32.top", {"start": v(282.97, -165.7) * mm, "end": v(283.97, -165.7) * mm});
            skLineSegment(sketch, "E32.right", {"start": v(283.97, -45.7) * mm, "end": v(283.97, -165.7) * mm});
            skLineSegment(sketch, "E33", {"start": v(284.17, -45.7) * mm, "end": v(284.17, -165.7) * mm, "construction": true});
            skLineSegment(sketch, "E34", {"start": v(309.17, -45.7) * mm, "end": v(309.17, -165.7) * mm, "construction": true});
            skLineSegment(sketch, "E35", {"start": v(284.17, -112.21) * mm, "end": v(309.17, -112.21) * mm, "construction": true});
            skLineSegment(sketch, "E36", {"start": v(335.57, -45.7) * mm, "end": v(335.57, -119.57) * mm, "construction": true});
            skLineSegment(sketch, "E37", {"start": v(310.57, -45.7) * mm, "end": v(310.57, -165.7) * mm, "construction": true});
            skLineSegment(sketch, "E38", {"start": v(336.97, -45.7) * mm, "end": v(336.97, -165.7) * mm, "construction": true});
            skLineSegment(sketch, "E39", {"start": v(361.97, -45.7) * mm, "end": v(361.97, -165.7) * mm, "construction": true});
            skLineSegment(sketch, "E40", {"start": v(310.57, -111.1) * mm, "end": v(335.57, -111.1) * mm, "construction": true});
            skLineSegment(sketch, "E41", {"start": v(336.97, -111.1) * mm, "end": v(361.97, -111.1) * mm, "construction": true});
            skSolve(sketch);
        }
        {
            var Q0;
            {var subQ0=sQuery(id+"F11.wireOp",EDGE,"E28.left");Q0=makeQuery(id+"F11.imprint","IMPRINT",FACE,{"disambiguationData":[TD([[makeQuery(id+"F11.imprint","IMPRINT",EDGE,{"derivedFrom":subQ0}),1.0]])]});}
            var Q1;
            {var subQ0=sQuery(id+"F11.wireOp",EDGE,"E29.left");Q1=makeQuery(id+"F11.imprint","IMPRINT",FACE,{"disambiguationData":[TD([[makeQuery(id+"F11.imprint","IMPRINT",EDGE,{"derivedFrom":subQ0}),-1.0]])]});}
            var Q2;
            {var subQ2=sQuery(id+"F11.wireOp",EDGE,"E29.left");Q2=makeQuery(id+"F11.imprint","IMPRINT",FACE,{"disambiguationData":[TD([[makeQuery(id+"F11.imprint","IMPRINT",EDGE,{"derivedFrom":subQ2}),1.0]])]});}
            var Q3;
            {var subQ0=sQuery(id+"F11.wireOp",EDGE,"E29.right");Q3=makeQuery(id+"F11.imprint","IMPRINT",FACE,{"disambiguationData":[TD([[makeQuery(id+"F11.imprint","IMPRINT",EDGE,{"derivedFrom":subQ0}),1.0]])]});}
            var Q4;
            {var subQ2=sQuery(id+"F11.wireOp",EDGE,"E30.left");Q4=makeQuery(id+"F11.imprint","IMPRINT",FACE,{"disambiguationData":[TD([[makeQuery(id+"F11.imprint","IMPRINT",EDGE,{"derivedFrom":subQ2}),1.0]])]});}
            var Q5;
            {var subQ0=sQuery(id+"F11.wireOp",EDGE,"E30.right");Q5=makeQuery(id+"F11.imprint","IMPRINT",FACE,{"disambiguationData":[TD([[makeQuery(id+"F11.imprint","IMPRINT",EDGE,{"derivedFrom":subQ0}),1.0]])]});}
            var Q6;
            {var subQ0=sQuery(id+"F11.wireOp",EDGE,"E28.right");Q6=makeQuery(id+"F11.imprint","IMPRINT",FACE,{"disambiguationData":[TD([[makeQuery(id+"F11.imprint","IMPRINT",EDGE,{"derivedFrom":subQ0}),-1.0]])]});}
            extrude(context, id + "F12", {"entities" : qUnion([Q0, Q1, Q2, Q3, Q4, Q5, Q6]), "depth" : 1 * mm, "offsetDistance" : 25 * mm});
        }
        {
            var Q0;
            {var subQ0=sQuery(id+"F11.wireOp",EDGE,"E28.left");Q0=makeQuery(id+"F11.imprint","IMPRINT",FACE,{"disambiguationData":[TD([[makeQuery(id+"F11.imprint","IMPRINT",EDGE,{"derivedFrom":subQ0}),1.0]])]});}
            var Q1;
            {var subQ2=sQuery(id+"F11.wireOp",EDGE,"E29.left");Q1=makeQuery(id+"F11.imprint","IMPRINT",FACE,{"disambiguationData":[TD([[makeQuery(id+"F11.imprint","IMPRINT",EDGE,{"derivedFrom":subQ2}),1.0]])]});}
            var Q2;
            {var subQ2=sQuery(id+"F11.wireOp",EDGE,"E30.left");Q2=makeQuery(id+"F11.imprint","IMPRINT",FACE,{"disambiguationData":[TD([[makeQuery(id+"F11.imprint","IMPRINT",EDGE,{"derivedFrom":subQ2}),1.0]])]});}
            var Q3;
            {var subQ0=sQuery(id+"F11.wireOp",EDGE,"E28.right");Q3=makeQuery(id+"F11.imprint","IMPRINT",FACE,{"disambiguationData":[TD([[makeQuery(id+"F11.imprint","IMPRINT",EDGE,{"derivedFrom":subQ0}),-1.0]])]});}
            extrude(context, id + "F13", {"entities" : qUnion([Q0, Q1, Q2, Q3]), "operationType" : NewBodyOperationType.ADD, "depth" : 10 * mm, "offsetDistance" : 25 * mm});
        }
        {
            var Q0;
            Q0=makeQuery(id+"F13.opExtrude","SWEPT_FACE",FACE,{"disambiguationData":[OSD([sQuery(id+"F11.wireOp",EDGE,"E32.right")])]});
            var sketch = newSketch(context, id + "F14", { "sketchPlane" : qUnion([Q0])});
            skLineSegment(sketch, "E42", {"start": v(-60.3, 1) * mm, "end": v(-47.45, 10) * mm});
            skLineSegment(sketch, "E43", {"start": v(-47.45, 10) * mm, "end": v(-45.7, 10) * mm});
            skLineSegment(sketch, "E44", {"start": v(-45.7, 10) * mm, "end": v(-58.56, 1) * mm});
            skLineSegment(sketch, "E45", {"start": v(-58.56, 1) * mm, "end": v(-60.3, 1) * mm});
            skLineSegment(sketch, "E46.1.0.0", {"start": v(-79.48, 1) * mm, "end": v(-66.62, 10) * mm});
            skLineSegment(sketch, "E46.1.0.1", {"start": v(-64.88, 10) * mm, "end": v(-77.73, 1) * mm});
            skLineSegment(sketch, "E46.1.0.2", {"start": v(-66.62, 10) * mm, "end": v(-64.88, 10) * mm});
            skLineSegment(sketch, "E46.1.0.3", {"start": v(-77.73, 1) * mm, "end": v(-79.48, 1) * mm});
            skLineSegment(sketch, "E46.2.0.0", {"start": v(-98.65, 1) * mm, "end": v(-85.8, 10) * mm});
            skLineSegment(sketch, "E46.2.0.1", {"start": v(-84.06, 10) * mm, "end": v(-96.91, 1) * mm});
            skLineSegment(sketch, "E46.2.0.2", {"start": v(-85.8, 10) * mm, "end": v(-84.06, 10) * mm});
            skLineSegment(sketch, "E46.2.0.3", {"start": v(-96.91, 1) * mm, "end": v(-98.65, 1) * mm});
            skLineSegment(sketch, "E46.direction1", {"start": v(-60.3, 1) * mm, "end": v(-79.48, 1) * mm, "construction": true});
            skLineSegment(sketch, "E47.0.3.0", {"start": v(-117.83, 1) * mm, "end": v(-104.98, 10) * mm});
            skLineSegment(sketch, "E47.3.3.0", {"start": v(-103.24, 10) * mm, "end": v(-116.09, 1) * mm});
            skLineSegment(sketch, "E47.6.3.0", {"start": v(-104.98, 10) * mm, "end": v(-103.24, 10) * mm});
            skLineSegment(sketch, "E47.9.3.0", {"start": v(-116.09, 1) * mm, "end": v(-117.83, 1) * mm});
            skLineSegment(sketch, "E48.0.4.0", {"start": v(-137.01, 1) * mm, "end": v(-124.16, 10) * mm});
            skLineSegment(sketch, "E48.3.4.0", {"start": v(-122.41, 10) * mm, "end": v(-135.27, 1) * mm});
            skLineSegment(sketch, "E48.6.4.0", {"start": v(-124.16, 10) * mm, "end": v(-122.41, 10) * mm});
            skLineSegment(sketch, "E48.9.4.0", {"start": v(-135.27, 1) * mm, "end": v(-137.01, 1) * mm});
            skLineSegment(sketch, "E48.0.5.0", {"start": v(-156.19, 1) * mm, "end": v(-143.33, 10) * mm});
            skLineSegment(sketch, "E48.3.5.0", {"start": v(-141.6, 10) * mm, "end": v(-154.44, 1) * mm});
            skLineSegment(sketch, "E48.6.5.0", {"start": v(-143.33, 10) * mm, "end": v(-141.6, 10) * mm});
            skLineSegment(sketch, "E48.9.5.0", {"start": v(-154.44, 1) * mm, "end": v(-156.19, 1) * mm});
            skSolve(sketch);
        }
        {
            var Q0;
            Q0=makeQuery(id+"F14.imprint","IMPRINT",FACE,{"disambiguationData":[TD([[makeQuery(id+"F14.imprint","IMPRINT",EDGE,{"derivedFrom":sQuery(id+"F14.wireOp",EDGE,"E42")}),-1.0]])]});
            var Q1;
            Q1=makeQuery(id+"F14.imprint","IMPRINT",FACE,{"disambiguationData":[TD([[makeQuery(id+"F14.imprint","IMPRINT",EDGE,{"derivedFrom":sQuery(id+"F14.wireOp",EDGE,"E46.1.0.0")}),-1.0]])]});
            var Q2;
            Q2=makeQuery(id+"F14.imprint","IMPRINT",FACE,{"disambiguationData":[TD([[makeQuery(id+"F14.imprint","IMPRINT",EDGE,{"derivedFrom":sQuery(id+"F14.wireOp",EDGE,"E46.2.0.0")}),-1.0]])]});
            var Q3;
            Q3=makeQuery(id+"F14.imprint","IMPRINT",FACE,{"disambiguationData":[TD([[makeQuery(id+"F14.imprint","IMPRINT",EDGE,{"derivedFrom":sQuery(id+"F14.wireOp",EDGE,"E47.0.3.0")}),-1.0]])]});
            var Q4;
            Q4=makeQuery(id+"F14.imprint","IMPRINT",FACE,{"disambiguationData":[TD([[makeQuery(id+"F14.imprint","IMPRINT",EDGE,{"derivedFrom":sQuery(id+"F14.wireOp",EDGE,"E48.0.4.0")}),-1.0]])]});
            var Q5;
            Q5=makeQuery(id+"F14.imprint","IMPRINT",FACE,{"disambiguationData":[TD([[makeQuery(id+"F14.imprint","IMPRINT",EDGE,{"derivedFrom":sQuery(id+"F14.wireOp",EDGE,"E48.0.5.0")}),-1.0]])]});
            var Q6;
            Q6=makeQuery(id+"F13.opExtrude","SWEPT_FACE",FACE,{"disambiguationData":[OSD([sQuery(id+"F11.wireOp",EDGE,"E31.right")])]});
            extrude(context, id + "F15", {"entities" : qUnion([Q0, Q1, Q2, Q3, Q4, Q5]), "operationType" : NewBodyOperationType.ADD, "endBound" : BoundingType.UP_TO_SURFACE, "depth" : 25 * mm, "endBoundEntityFace" : qUnion([Q6]), "offsetDistance" : 25 * mm});
        }
    });
